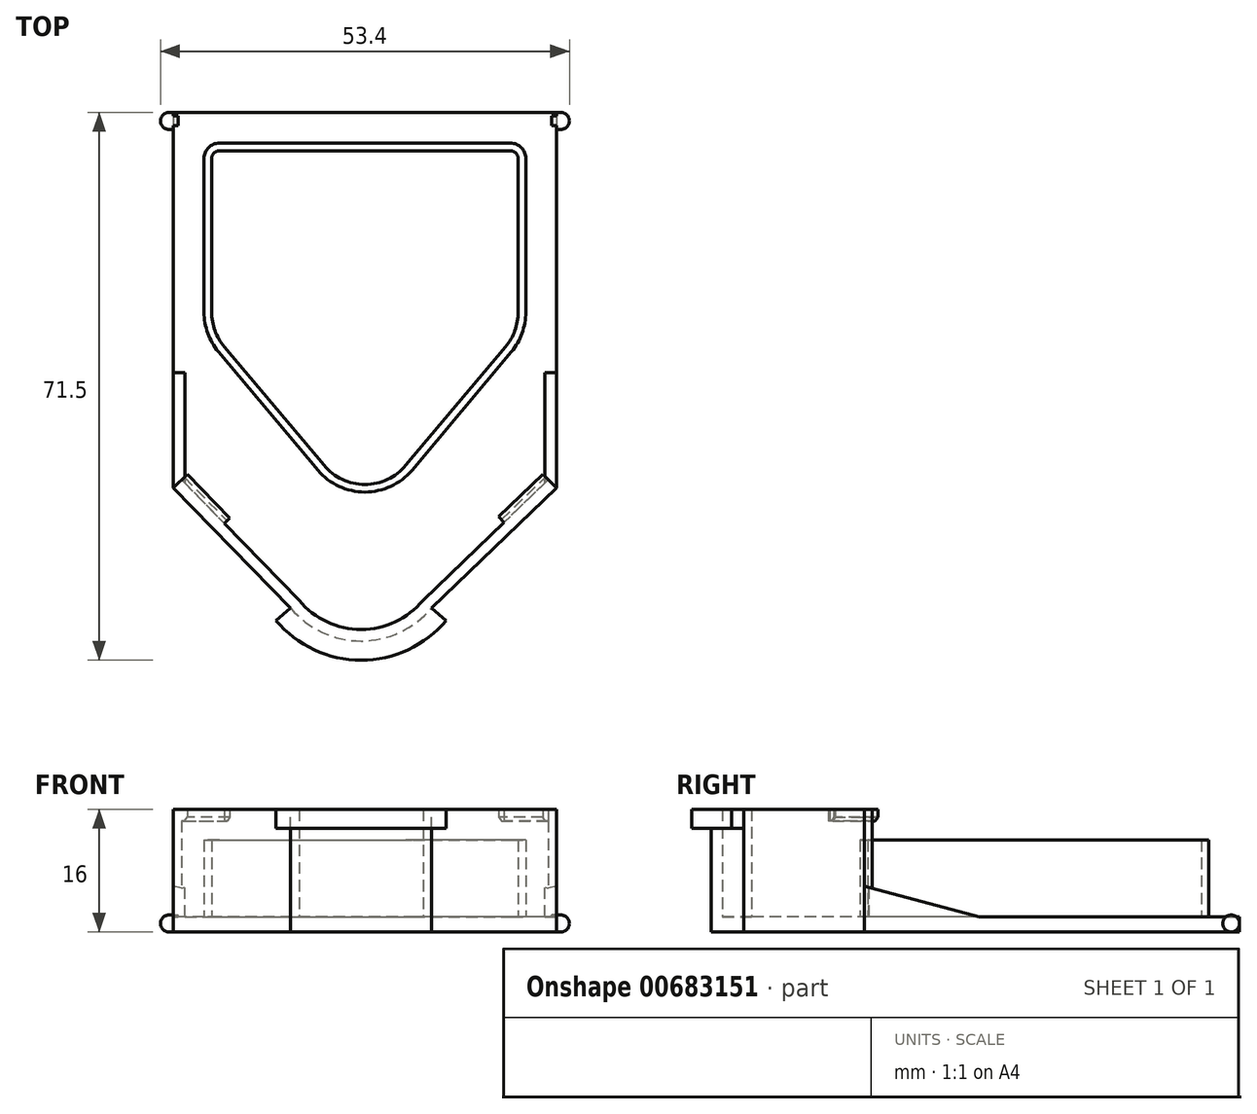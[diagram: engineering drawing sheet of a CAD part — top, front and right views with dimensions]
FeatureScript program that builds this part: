
annotation { "Feature Type Name" : "Feature", "Feature Type Description" : "" }
export const myFeature = defineFeature(function(context is Context, id is Id, definition is map)
    precondition{}
    {
        {
            var Q0;
            Q0=qCreatedBy(makeId("Top.planeOp"),FACE);
            var sketch = newSketch(context, id + "F0", { "sketchPlane" : qUnion([Q0])});
            skLineSegment(sketch, "E0", {"start": v(2, 0) * mm, "end": v(40, 0) * mm});
            skLineSegment(sketch, "E1", {"start": v(42, -2) * mm, "end": v(42, -22.09) * mm});
            skLineSegment(sketch, "E2", {"start": v(21, 0) * mm, "end": v(21, -50) * mm});
            skLineSegment(sketch, "E3", {"start": v(40.13, -27.23) * mm, "end": v(27.13, -42.7) * mm});
            skLineSegment(sketch, "E4", {"start": v(0, -22.09) * mm, "end": v(0, -2) * mm});
            skPoint(sketch, "E4.startSnap0", {"position": v(21, -25) * mm});
            skLineSegment(sketch, "E5", {"start": v(1.87, -27.23) * mm, "end": v(14.87, -42.7) * mm});
            skPoint(sketch, "E6.visualSharp", {"position": v(0, -25) * mm});
            skArc(sketch, "E6.filletArc", {"start": v(0, -22.09) * mm, "mid": v(0.48, -24.82) * mm, "end": v(1.87, -27.23) * mm});
            skPoint(sketch, "E7.visualSharp", {"position": v(42, -25) * mm});
            skArc(sketch, "E7.filletArc", {"start": v(40.13, -27.23) * mm, "mid": v(41.52, -24.82) * mm, "end": v(42, -22.09) * mm});
            skPoint(sketch, "E8.visualSharp", {"position": v(21, -50) * mm});
            skArc(sketch, "E8.filletArc", {"start": v(14.87, -42.7) * mm, "mid": v(21, -45.56) * mm, "end": v(27.13, -42.7) * mm});
            skPoint(sketch, "E9.visualSharp", {"position": v(0, 0) * mm});
            skArc(sketch, "E9.filletArc", {"start": v(2, 0) * mm, "mid": v(0.59, -0.59) * mm, "end": v(0, -2) * mm});
            skPoint(sketch, "E10.visualSharp", {"position": v(42, 0) * mm});
            skArc(sketch, "E10.filletArc", {"start": v(42, -2) * mm, "mid": v(41.41, -0.59) * mm, "end": v(40, 0) * mm});
            skArc(sketch, "E11.0", {"start": v(1, -22.09) * mm, "mid": v(1.42, -24.48) * mm, "end": v(2.64, -26.59) * mm});
            skLineSegment(sketch, "E11.1", {"start": v(2.64, -26.59) * mm, "end": v(15.64, -42.06) * mm});
            skLineSegment(sketch, "E11.2", {"start": v(1, -22.09) * mm, "end": v(1, -2) * mm});
            skArc(sketch, "E11.3", {"start": v(15.64, -42.06) * mm, "mid": v(21, -44.56) * mm, "end": v(26.36, -42.06) * mm});
            skLineSegment(sketch, "E11.4", {"start": v(2, -1) * mm, "end": v(40, -1) * mm});
            skLineSegment(sketch, "E11.5", {"start": v(41, -2) * mm, "end": v(41, -22.09) * mm});
            skArc(sketch, "E11.6", {"start": v(39.36, -26.59) * mm, "mid": v(40.58, -24.48) * mm, "end": v(41, -22.09) * mm});
            skLineSegment(sketch, "E11.7", {"start": v(39.36, -26.59) * mm, "end": v(26.36, -42.06) * mm});
            skPoint(sketch, "E12.visualSharp", {"position": v(1, -1) * mm});
            skArc(sketch, "E12.filletArc", {"start": v(2, -1) * mm, "mid": v(1.3, -1.3) * mm, "end": v(1, -2) * mm});
            skPoint(sketch, "E13.visualSharp", {"position": v(41, -1) * mm});
            skArc(sketch, "E13.filletArc", {"start": v(41, -2) * mm, "mid": v(40.7, -1.3) * mm, "end": v(40, -1) * mm});
            skSolve(sketch);
        }
        {
            var Q0;
            Q0 = qSketchRegion(id + "F0", true);
            extrude(context, id + "F1", {"entities" : qUnion([Q0]), "depth" : 10 * mm, "offsetDistance" : 25 * mm});
        }
        {
            var Q0;
            Q0=qCreatedBy(makeId("Top.planeOp"),FACE);
            var sketch = newSketch(context, id + "F2", { "sketchPlane" : qUnion([Q0])});
            skLineSegment(sketch, "E14.0", {"start": v(40.13, -27.23) * mm, "end": v(27.13, -42.7) * mm});
            skArc(sketch, "E15.0", {"start": v(14.87, -42.7) * mm, "mid": v(21, -45.56) * mm, "end": v(27.13, -42.7) * mm});
            skLineSegment(sketch, "E16.0", {"start": v(1.87, -27.23) * mm, "end": v(14.87, -42.7) * mm});
            skLineSegment(sketch, "E17.bottom", {"start": v(46, 4) * mm, "end": v(-4, 4) * mm});
            skLineSegment(sketch, "E17.left", {"start": v(46, 4) * mm, "end": v(46, -45) * mm});
            skLineSegment(sketch, "E17.right", {"start": v(-4, 4) * mm, "end": v(-4, -45) * mm});
            skPoint(sketch, "E18.0", {"position": v(42, -12.04) * mm});
            skLineSegment(sketch, "E19.0", {"start": v(2, 0) * mm, "end": v(40, 0) * mm});
            skLineSegment(sketch, "E20.0", {"start": v(0, -22.09) * mm, "end": v(0, -2) * mm});
            skPoint(sketch, "E21.visualSharp", {"position": v(21, -68.66) * mm});
            skArc(sketch, "E21.filletArc", {"start": v(11.31, -60.72) * mm, "mid": v(20.5, -65) * mm, "end": v(29.69, -60.72) * mm});
            skLineSegment(sketch, "E22", {"start": v(-4, -45) * mm, "end": v(11.31, -60.72) * mm});
            skLineSegment(sketch, "E23", {"start": v(46, -45) * mm, "end": v(29.69, -60.72) * mm});
            skSolve(sketch);
        }
        {
            var Q0;
            Q0 = qSketchRegion(id + "F2", true);
            extrude(context, id + "F3", {"entities" : qUnion([Q0]), "operationType" : NewBodyOperationType.ADD, "oppositeDirection" : true, "depth" : 2 * mm, "offsetDistance" : 25 * mm});
        }
        {
            var Q0;
            Q0=makeQuery(id+"F3.opExtrude","SWEPT_FACE",FACE,{"disambiguationData":[OSD([sQuery(id+"F2.wireOp",EDGE,"E17.left")])]});
            var sketch = newSketch(context, id + "F4", { "sketchPlane" : qUnion([Q0])});
            skCircle(sketch, "E24", {"center": v(2.9, -0.9) * mm, "radius": 1.1 * mm});
            skPoint(sketch, "E24.first.point", {"position": v(2.9, -2) * mm});
            skPoint(sketch, "E24.second.point", {"position": v(4, -0.9) * mm});
            skPoint(sketch, "E24.third.point", {"position": v(2.6, 0.16) * mm});
            skSolve(sketch);
        }
        {
            var Q0;
            Q0 = qSketchRegion(id + "F4", true);
            extrude(context, id + "F5", {"entities" : qUnion([Q0]), "operationType" : NewBodyOperationType.ADD, "endBound" : BoundingType.SYMMETRIC, "depth" : 1.2 * mm, "offsetDistance" : 25 * mm});
        }
        {
            var Q0;
            Q0=makeQuery(id+"F3.opExtrude","SWEPT_FACE",FACE,{"disambiguationData":[OSD([sQuery(id+"F2.wireOp",EDGE,"E17.right")])]});
            var sketch = newSketch(context, id + "F6", { "sketchPlane" : qUnion([Q0])});
            skCircle(sketch, "E25", {"center": v(-2.9, -0.9) * mm, "radius": 1.1 * mm});
            skPoint(sketch, "E25.first.point", {"position": v(-2.9, -2) * mm});
            skPoint(sketch, "E25.second.point", {"position": v(-4, -0.9) * mm});
            skPoint(sketch, "E25.third.point", {"position": v(-2.19, -0.06) * mm});
            skSolve(sketch);
        }
        {
            var Q0;
            Q0 = qSketchRegion(id + "F6", true);
            extrude(context, id + "F7", {"entities" : qUnion([Q0]), "operationType" : NewBodyOperationType.ADD, "endBound" : BoundingType.SYMMETRIC, "depth" : 1.2 * mm, "offsetDistance" : 25 * mm});
        }
        {
            var Q0;
            Q0=makeQuery(id+"F7.opExtrude","CAP_FACE",FACE,{"disambiguationData":[OSD([sQuery(id+"F6.wireOp",EDGE,"E25")])],"isStart":false});
            var sketch = newSketch(context, id + "F8", { "sketchPlane" : qUnion([Q0])});
            skCircle(sketch, "E26.0.0", {"center": v(-2.9, -0.9) * mm, "radius": 1.1 * mm});
            skLineSegment(sketch, "E27", {"start": v(-2.9, -2) * mm, "end": v(-2.9, 0.2) * mm});
            skSolve(sketch);
        }
        {
            var Q0;
            {var subQ0=sQuery(id+"F8.wireOp",EDGE,"E27");Q0=makeQuery(id+"F8.imprint","IMPRINT",FACE,{"disambiguationData":[TD([[makeQuery(id+"F8.imprint","IMPRINT",EDGE,{"derivedFrom":subQ0}),1.0]])]});}
            var Q1;
            Q1=sQuery(id+"F8.wireOp",EDGE,"E27");
            revolve(context, id + "F9", {"operationType" : NewBodyOperationType.ADD, "entities" : qUnion([Q0]), "axis" : qUnion([Q1]), "revolveType" : RevolveType.FULL});
        }
        {
            var Q0;
            Q0=makeQuery(id+"F5.opExtrude","CAP_FACE",FACE,{"disambiguationData":[OSD([sQuery(id+"F4.wireOp",EDGE,"E24")])],"isStart":false});
            var sketch = newSketch(context, id + "F10", { "sketchPlane" : qUnion([Q0])});
            skCircle(sketch, "E28.0", {"center": v(2.9, -0.9) * mm, "radius": 1.1 * mm});
            skLineSegment(sketch, "E29", {"start": v(2.9, -2) * mm, "end": v(2.9, 0.2) * mm});
            skSolve(sketch);
        }
        {
            var Q0;
            {var subQ0=sQuery(id+"F10.wireOp",EDGE,"E29");Q0=makeQuery(id+"F10.imprint","IMPRINT",FACE,{"disambiguationData":[TD([[makeQuery(id+"F10.imprint","IMPRINT",EDGE,{"derivedFrom":subQ0}),1.0]])]});}
            var Q1;
            Q1=sQuery(id+"F10.wireOp",EDGE,"E29");
            revolve(context, id + "F11", {"operationType" : NewBodyOperationType.ADD, "entities" : qUnion([Q0]), "axis" : qUnion([Q1]), "revolveType" : RevolveType.FULL});
        }
        {
            var Q0;
            {var subQ0=sQuery(id+"F2.wireOp",EDGE,"E23");var subQ1=sQuery(id+"F2.wireOp",EDGE,"E22");var subQ2=sQuery(id+"F2.wireOp",EDGE,"E17.right");var subQ3=sQuery(id+"F2.wireOp",EDGE,"E21.filletArc");var subQ4=sQuery(id+"F2.wireOp",EDGE,"E17.bottom");var subQ5=sQuery(id+"F2.wireOp",EDGE,"E17.left");Q0=makeQuery(id+"F3.boolean.opBoolean","SPLIT",FACE,{"disambiguationData":[TD([makeQuery(id+"F1.opExtrude","SWEPT_FACE",FACE,{"disambiguationData":[OSD([sQuery(id+"F0.wireOp",EDGE,"E0")])]})])],"derivedFrom":makeQuery(id+"F3.opExtrude","CAP_FACE",FACE,{"disambiguationData":[OSD([subQ4,subQ5,subQ2,subQ3,subQ1,subQ0])],"isStart":true})});}
            var sketch = newSketch(context, id + "F12", { "sketchPlane" : qUnion([Q0])});
            skLineSegment(sketch, "E30.0", {"start": v(-4, -45) * mm, "end": v(11.31, -60.72) * mm});
            skArc(sketch, "E31.0", {"start": v(11.31, -60.72) * mm, "mid": v(20.5, -65) * mm, "end": v(29.69, -60.72) * mm});
            skLineSegment(sketch, "E32.0", {"start": v(46, -45) * mm, "end": v(29.69, -60.72) * mm});
            skLineSegment(sketch, "E33.0", {"start": v(44.92, -43.95) * mm, "end": v(28.59, -59.7) * mm});
            skArc(sketch, "E33.1", {"start": v(12.43, -59.71) * mm, "mid": v(20.51, -63.5) * mm, "end": v(28.59, -59.7) * mm});
            skLineSegment(sketch, "E33.2", {"start": v(-2.93, -43.95) * mm, "end": v(12.43, -59.71) * mm});
            skLineSegment(sketch, "E34", {"start": v(-2.93, -43.95) * mm, "end": v(-4, -45) * mm});
            skLineSegment(sketch, "E35", {"start": v(44.92, -43.95) * mm, "end": v(46, -45) * mm});
            skSolve(sketch);
        }
        {
            var Q0;
            Q0=makeQuery(id+"F12.imprint","IMPRINT",FACE,{"disambiguationData":[TD([[makeQuery(id+"F12.imprint","IMPRINT",EDGE,{"derivedFrom":sQuery(id+"F12.wireOp",EDGE,"E30.0")}),1.0]])]});
            extrude(context, id + "F13", {"entities" : qUnion([Q0]), "operationType" : NewBodyOperationType.ADD, "depth" : 14 * mm, "offsetDistance" : 25 * mm});
        }
        {
            var Q0;
            Q0=makeQuery(id+"F13.opExtrude","SWEPT_FACE",FACE,{"disambiguationData":[OSD([sQuery(id+"F12.wireOp",EDGE,"E33.0")])]});
            var sketch = newSketch(context, id + "F14", { "sketchPlane" : qUnion([Q0])});
            skLineSegment(sketch, "E36.bottom", {"start": v(-1.85, 14) * mm, "end": v(6.15, 14) * mm});
            skLineSegment(sketch, "E36.top", {"start": v(-1.85, 12.5) * mm, "end": v(6.15, 12.5) * mm});
            skLineSegment(sketch, "E36.left", {"start": v(-1.85, 14) * mm, "end": v(-1.85, 12.5) * mm});
            skLineSegment(sketch, "E36.right", {"start": v(6.15, 14) * mm, "end": v(6.15, 12.5) * mm});
            skSolve(sketch);
        }
        {
            var Q0;
            Q0 = qSketchRegion(id + "F14", true);
            extrude(context, id + "F15", {"entities" : qUnion([Q0]), "operationType" : NewBodyOperationType.ADD, "depth" : 1 * mm, "offsetDistance" : 25 * mm});
        }
        {
            var Q0;
            Q0=makeQuery(id+"F15.opExtrude","CAP_EDGE",EDGE,{"disambiguationData":[OSD([sQuery(id+"F14.wireOp",EDGE,"E36.top")])],"isStart":false});
            chamfer(context, id + "F16", {"entities" : qUnion([Q0]), "width" : .5 * mm, "tangentPropagation" : true});
        }
        {
            var Q0;
            Q0=makeQuery(id+"F13.opExtrude","SWEPT_FACE",FACE,{"disambiguationData":[OSD([sQuery(id+"F12.wireOp",EDGE,"E33.2")])]});
            var sketch = newSketch(context, id + "F17", { "sketchPlane" : qUnion([Q0])});
            skLineSegment(sketch, "E37.bottom", {"start": v(-29.44, 14) * mm, "end": v(-37.44, 14) * mm});
            skLineSegment(sketch, "E37.top", {"start": v(-29.44, 12.5) * mm, "end": v(-37.44, 12.5) * mm});
            skLineSegment(sketch, "E37.left", {"start": v(-29.44, 14) * mm, "end": v(-29.44, 12.5) * mm});
            skLineSegment(sketch, "E37.right", {"start": v(-37.44, 14) * mm, "end": v(-37.44, 12.5) * mm});
            skSolve(sketch);
        }
        {
            var Q0;
            Q0 = qSketchRegion(id + "F17", true);
            extrude(context, id + "F18", {"entities" : qUnion([Q0]), "operationType" : NewBodyOperationType.ADD, "depth" : 1 * mm, "offsetDistance" : 25 * mm});
        }
        {
            var Q0;
            Q0=makeQuery(id+"F18.opExtrude","CAP_EDGE",EDGE,{"disambiguationData":[OSD([sQuery(id+"F17.wireOp",EDGE,"E37.top")])],"isStart":false});
            chamfer(context, id + "F19", {"entities" : qUnion([Q0]), "width" : .5 * mm, "tangentPropagation" : true});
        }
        {
            var Q0;
            Q0=makeQuery(id+"F18.boolean.opBoolean","MERGE",FACE,{"derivedFrom":[makeQuery(id+"F15.boolean.opBoolean","MERGE",FACE,{"derivedFrom":[makeQuery(id+"F13.opExtrude","CAP_FACE",FACE,{"disambiguationData":[OSD([sQuery(id+"F12.wireOp",EDGE,"E30.0"),sQuery(id+"F12.wireOp",EDGE,"E31.0"),sQuery(id+"F12.wireOp",EDGE,"E32.0"),sQuery(id+"F12.wireOp",EDGE,"E33.0"),sQuery(id+"F12.wireOp",EDGE,"E33.1"),sQuery(id+"F12.wireOp",EDGE,"E33.2"),sQuery(id+"F12.wireOp",EDGE,"E34"),sQuery(id+"F12.wireOp",EDGE,"E35")])],"isStart":false}),makeQuery(id+"F15.opExtrude","SWEPT_FACE",FACE,{"disambiguationData":[OSD([sQuery(id+"F14.wireOp",EDGE,"E36.bottom")])]})]}),makeQuery(id+"F18.opExtrude","SWEPT_FACE",FACE,{"disambiguationData":[OSD([sQuery(id+"F17.wireOp",EDGE,"E37.bottom")])]})]});
            var sketch = newSketch(context, id + "F20", { "sketchPlane" : qUnion([Q0])});
            skArc(sketch, "E38.0", {"start": v(11.31, -60.72) * mm, "mid": v(20.5, -65) * mm, "end": v(29.69, -60.72) * mm});
            skArc(sketch, "E39.0", {"start": v(9.4, -62.33) * mm, "mid": v(20.5, -67.5) * mm, "end": v(31.6, -62.33) * mm});
            skLineSegment(sketch, "E40", {"start": v(11.31, -60.72) * mm, "end": v(9.4, -62.33) * mm});
            skLineSegment(sketch, "E41", {"start": v(29.69, -60.72) * mm, "end": v(31.6, -62.33) * mm});
            skSolve(sketch);
        }
        {
            var Q0;
            Q0 = qSketchRegion(id + "F20", true);
            extrude(context, id + "F21", {"entities" : qUnion([Q0]), "operationType" : NewBodyOperationType.ADD, "oppositeDirection" : true, "depth" : 2.5 * mm, "offsetDistance" : 25 * mm});
        }
        {
            var Q0;
            {var subQ0=sQuery(id+"F2.wireOp",EDGE,"E17.left");var subQ1=makeQuery(id+"F3.opExtrude","SWEPT_FACE",FACE,{"disambiguationData":[OSD([subQ0])]});var subQ2=sQuery(id+"F2.wireOp",EDGE,"E23");var subQ3=sQuery(id+"F2.wireOp",EDGE,"E22");var subQ4=sQuery(id+"F2.wireOp",EDGE,"E21.filletArc");var subQ5=sQuery(id+"F2.wireOp",EDGE,"E17.right");var subQ6=sQuery(id+"F2.wireOp",EDGE,"E17.bottom");Q0=makeQuery(id+"F5.boolean.opBoolean","SPLIT",FACE,{"disambiguationData":[TD([makeQuery(id+"F3.opExtrude","CAP_FACE",FACE,{"disambiguationData":[OSD([subQ6,subQ0,subQ5,subQ4,subQ3,subQ2])],"isStart":true}),makeQuery(id+"F3.opExtrude","CAP_FACE",FACE,{"disambiguationData":[OSD([subQ6,subQ0,subQ5,subQ4,subQ3,subQ2])],"isStart":false}),subQ1,makeQuery(id+"F3.opExtrude","SWEPT_FACE",FACE,{"disambiguationData":[OSD([subQ2])]}),makeQuery(id+"F5.opExtrude","SWEPT_FACE",FACE,{"disambiguationData":[OSD([sQuery(id+"F4.wireOp",EDGE,"E24")])]})])],"derivedFrom":subQ1});}
            var sketch = newSketch(context, id + "F22", { "sketchPlane" : qUnion([Q0])});
            skLineSegment(sketch, "E42", {"start": v(-45, 0) * mm, "end": v(-45, 4) * mm});
            skLineSegment(sketch, "E43", {"start": v(-45, 4) * mm, "end": v(-30, 0) * mm});
            skLineSegment(sketch, "E44", {"start": v(-30, 0) * mm, "end": v(-45, 0) * mm});
            skSolve(sketch);
        }
        {
            var Q0;
            Q0=makeQuery(id+"F22.imprint","IMPRINT",FACE,{"disambiguationData":[TD([[makeQuery(id+"F22.imprint","IMPRINT",EDGE,{"derivedFrom":sQuery(id+"F22.wireOp",EDGE,"E42")}),-1.0]])]});
            var Q1;
            Q1=makeQuery(id+"F13.opExtrude","SWEPT_FACE",FACE,{"disambiguationData":[OSD([sQuery(id+"F12.wireOp",EDGE,"E33.0")])]});
            var Q2;
            Q2=makeQuery(id+"F13.opExtrude","CAP_VERTEX",VERTEX,{"disambiguationData":[OSD([sQuery(id+"F12.wireOp",EDGE,"E33.0"),sQuery(id+"F12.wireOp",EDGE,"E35")])],"isStart":true});
            extrude(context, id + "F23", {"entities" : qUnion([Q0]), "operationType" : NewBodyOperationType.ADD, "oppositeDirection" : true, "depth" : 1.5 * mm, "endBoundEntityFace" : qUnion([Q1]), "endBoundEntityVertex" : qUnion([Q2]), "offsetDistance" : 25 * mm});
        }
        {
            var Q0;
            {var subQ0=sQuery(id+"F2.wireOp",EDGE,"E17.right");var subQ1=makeQuery(id+"F3.opExtrude","SWEPT_FACE",FACE,{"disambiguationData":[OSD([subQ0])]});var subQ2=sQuery(id+"F2.wireOp",EDGE,"E23");var subQ3=sQuery(id+"F2.wireOp",EDGE,"E22");var subQ4=sQuery(id+"F2.wireOp",EDGE,"E21.filletArc");var subQ5=sQuery(id+"F2.wireOp",EDGE,"E17.left");var subQ6=sQuery(id+"F2.wireOp",EDGE,"E17.bottom");Q0=makeQuery(id+"F7.boolean.opBoolean","SPLIT",FACE,{"disambiguationData":[TD([makeQuery(id+"F3.opExtrude","CAP_FACE",FACE,{"disambiguationData":[OSD([subQ6,subQ5,subQ0,subQ4,subQ3,subQ2])],"isStart":true}),makeQuery(id+"F3.opExtrude","CAP_FACE",FACE,{"disambiguationData":[OSD([subQ6,subQ5,subQ0,subQ4,subQ3,subQ2])],"isStart":false}),subQ1,makeQuery(id+"F3.opExtrude","SWEPT_FACE",FACE,{"disambiguationData":[OSD([subQ3])]}),makeQuery(id+"F7.opExtrude","SWEPT_FACE",FACE,{"disambiguationData":[OSD([sQuery(id+"F6.wireOp",EDGE,"E25")])]})])],"derivedFrom":subQ1});}
            var sketch = newSketch(context, id + "F24", { "sketchPlane" : qUnion([Q0])});
            skLineSegment(sketch, "E45", {"start": v(45, 0) * mm, "end": v(45, 4) * mm});
            skLineSegment(sketch, "E46", {"start": v(45, 4) * mm, "end": v(30, 0) * mm});
            skLineSegment(sketch, "E47", {"start": v(30, 0) * mm, "end": v(45, 0) * mm});
            skSolve(sketch);
        }
        {
            var Q0;
            Q0=makeQuery(id+"F24.imprint","IMPRINT",FACE,{"disambiguationData":[TD([[makeQuery(id+"F24.imprint","IMPRINT",EDGE,{"derivedFrom":sQuery(id+"F24.wireOp",EDGE,"E45")}),1.0]])]});
            extrude(context, id + "F25", {"entities" : qUnion([Q0]), "operationType" : NewBodyOperationType.ADD, "oppositeDirection" : true, "depth" : 1.5 * mm, "offsetDistance" : 25 * mm});
        }
    });
